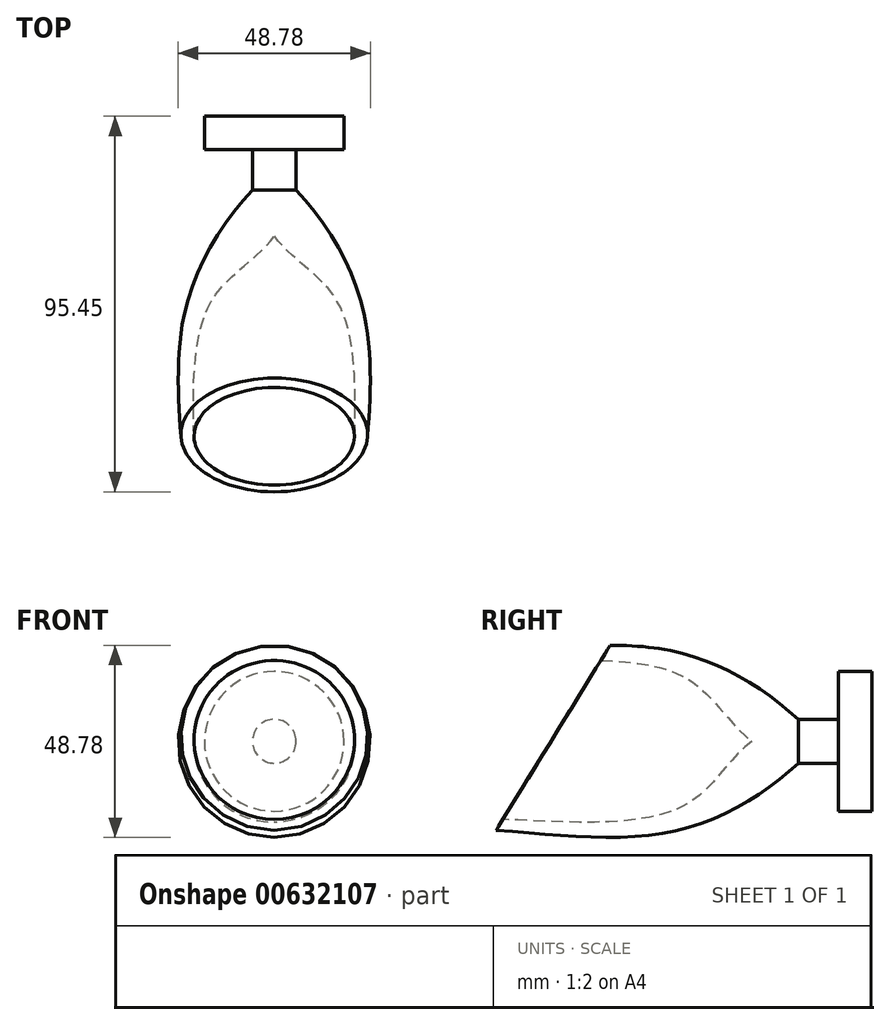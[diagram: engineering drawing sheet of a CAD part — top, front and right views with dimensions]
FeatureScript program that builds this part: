
annotation { "Feature Type Name" : "Feature", "Feature Type Description" : "" }
export const myFeature = defineFeature(function(context is Context, id is Id, definition is map)
    precondition{}
    {
        {
            var Q0;
            Q0=qCreatedBy(makeId("Front.planeOp"),FACE);
            var sketch = newSketch(context, id + "F0", { "sketchPlane" : qUnion([Q0])});
            skLineSegment(sketch, "E0.bottom", {"start": v(-27.26, 0) * mm, "end": v(42.17, 0) * mm});
            skLineSegment(sketch, "E0.top", {"start": v(-27.26, 65.18) * mm, "end": v(42.17, 65.18) * mm});
            skLineSegment(sketch, "E0.left", {"start": v(-27.26, 0) * mm, "end": v(-27.26, 65.18) * mm});
            skLineSegment(sketch, "E0.right", {"start": v(42.17, 0) * mm, "end": v(42.17, 65.18) * mm});
            skSolve(sketch);
        }
        {
            var Q0;
            Q0 = qSketchRegion(id + "F0", true);
            extrude(context, id + "F1", {"entities" : qUnion([Q0]), "depth" : 152.4 * mm, "offsetDistance" : 25.4 * mm});
        }
        {
            var Q0;
            Q0=makeQuery(id+"F1.opExtrude","SWEPT_FACE",FACE,{"disambiguationData":[OSD([sQuery(id+"F0.wireOp",EDGE,"E0.left")])]});
            var sketch = newSketch(context, id + "F2", { "sketchPlane" : qUnion([Q0])});
            skLineSegment(sketch, "E1", {"start": v(152.4, 0) * mm, "end": v(112.28, 65.18) * mm});
            skLineSegment(sketch, "E2", {"start": v(112.28, 65.18) * mm, "end": v(152.4, 65.18) * mm});
            skLineSegment(sketch, "E3", {"start": v(152.4, 65.18) * mm, "end": v(152.4, 0) * mm});
            skSolve(sketch);
        }
        {
            var Q0;
            Q0 = qSketchRegion(id + "F2", true);
            extrude(context, id + "F3", {"entities" : qUnion([Q0]), "operationType" : NewBodyOperationType.REMOVE, "endBound" : BoundingType.THROUGH_ALL, "oppositeDirection" : true, "depth" : 25.4 * mm, "offsetDistance" : 25.4 * mm});
        }
        {
            var Q0;
            Q0=qCreatedBy(makeId("Right.planeOp"),FACE);
            var sketch = newSketch(context, id + "F4", { "sketchPlane" : qUnion([Q0])});
            skLineSegment(sketch, "E4", {"start": v(7.58, 34.4) * mm, "end": v(-149.88, 34.4) * mm, "construction": true});
            skFitSpline(sketch, "E5", {"points": [v(-154.78, 12.39) * mm, v(-101.11, 11.32) * mm, v(-68.42, 28.84) * mm], "startDerivative": vector(110.19, -5) * mm, "endDerivative": vector(57.54, 53.14) * mm});
            skLineSegment(sketch, "E6", {"start": v(-68.42, 28.84) * mm, "end": v(-58.24, 28.84) * mm});
            skLineSegment(sketch, "E7", {"start": v(-58.24, 28.84) * mm, "end": v(-58.24, 16.65) * mm});
            skLineSegment(sketch, "E8", {"start": v(-58.24, 16.65) * mm, "end": v(-49.7, 16.65) * mm});
            skLineSegment(sketch, "E9", {"start": v(-49.7, 16.65) * mm, "end": v(-49.7, 34.4) * mm});
            skLineSegment(sketch, "E10", {"start": v(-49.7, 34.4) * mm, "end": v(-80.16, 34.4) * mm});
            skFitSpline(sketch, "E11", {"points": [v(-80.16, 34.4) * mm, v(-98.58, 17.45) * mm, v(-152.53, 14.85) * mm], "startDerivative": vector(-48.92, -35.27) * mm, "endDerivative": vector(-89.04, 1.23) * mm});
            skLineSegment(sketch, "E12", {"start": v(-152.53, 14.85) * mm, "end": v(-154.78, 12.39) * mm});
            skSolve(sketch);
        }
        {
            var Q0;
            Q0=makeQuery(id+"F4.imprint","IMPRINT",FACE,{"disambiguationData":[TD([[makeQuery(id+"F4.imprint","IMPRINT",EDGE,{"derivedFrom":sQuery(id+"F4.wireOp",EDGE,"E5")}),1.0]])]});
            var Q1;
            Q1=sQuery(id+"F4.wireOp",EDGE,"E4");
            revolve(context, id + "F5", {"operationType" : NewBodyOperationType.INTERSECT, "surfaceOperationType" : NewSurfaceOperationType.NEW, "entities" : qUnion([Q0]), "axis" : qUnion([Q1]), "revolveType" : RevolveType.FULL, "oppositeDirection" : true});
        }
    });
